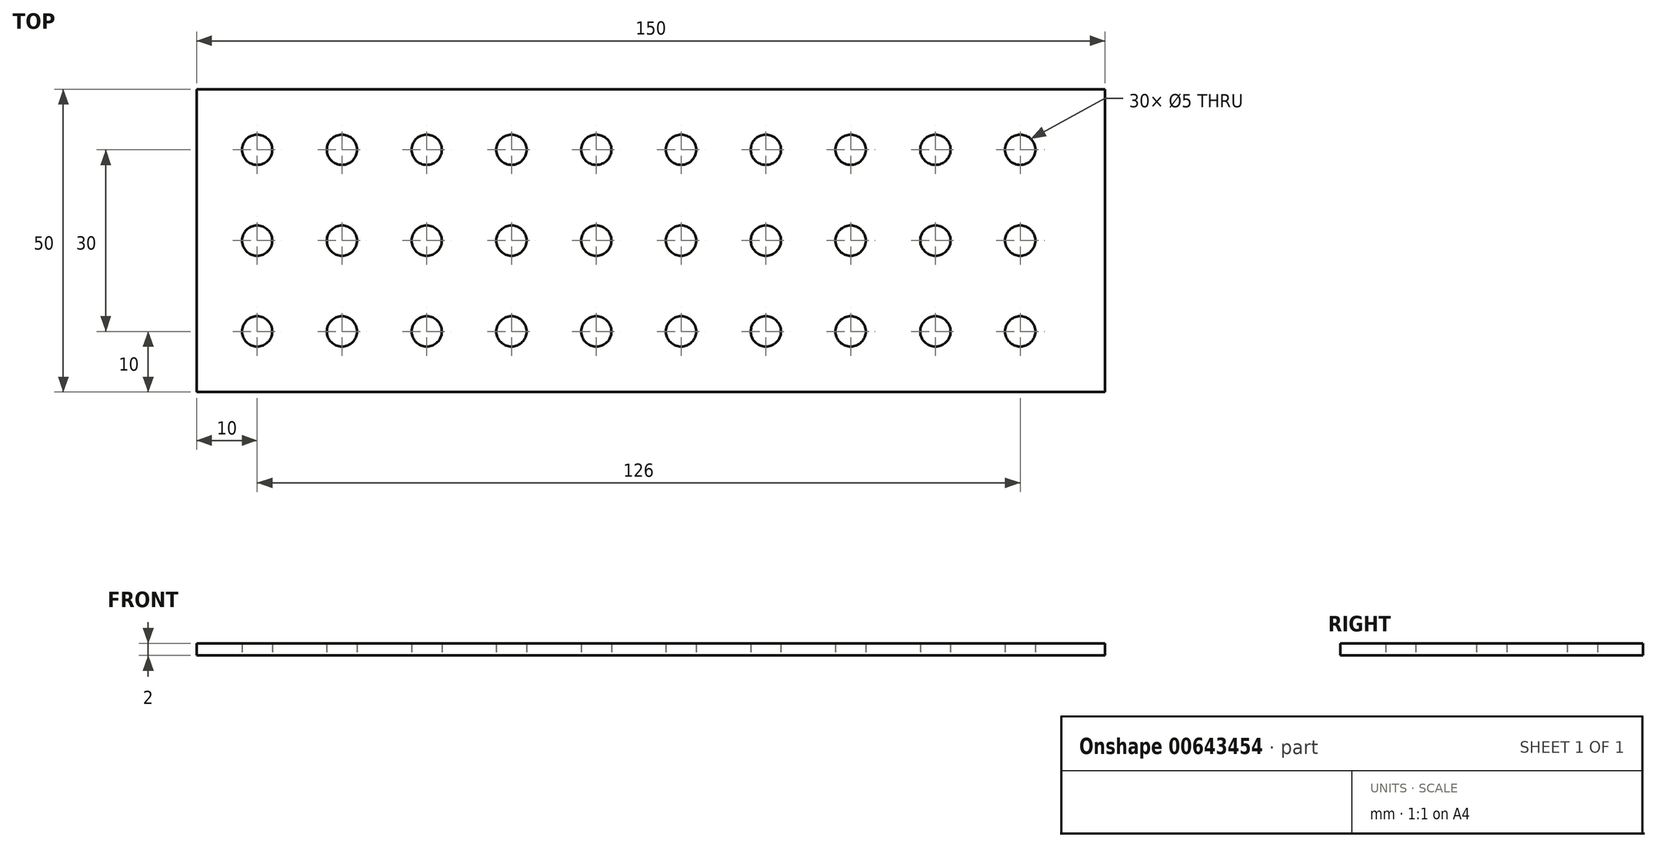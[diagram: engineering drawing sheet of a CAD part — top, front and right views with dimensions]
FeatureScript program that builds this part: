
annotation { "Feature Type Name" : "Feature", "Feature Type Description" : "" }
export const myFeature = defineFeature(function(context is Context, id is Id, definition is map)
    precondition{}
    {
        {
            var Q0;
            Q0=qCreatedBy(makeId("Top.planeOp"),FACE);
            var sketch = newSketch(context, id + "F0", { "sketchPlane" : qUnion([Q0])});
            skLineSegment(sketch, "E0.bottom", {"start": v(-75, 0) * mm, "end": v(75, 0) * mm});
            skLineSegment(sketch, "E0.top", {"start": v(-75, 50) * mm, "end": v(75, 50) * mm});
            skLineSegment(sketch, "E0.left", {"start": v(-75, 0) * mm, "end": v(-75, 50) * mm});
            skLineSegment(sketch, "E0.right", {"start": v(75, 0) * mm, "end": v(75, 50) * mm});
            skCircle(sketch, "E1", {"center": v(-65, 10) * mm, "radius": 2.5 * mm});
            skCircle(sketch, "E2.0.1.0", {"center": v(-65, 25) * mm, "radius": 2.5 * mm});
            skCircle(sketch, "E2.0.2.0", {"center": v(-65, 40) * mm, "radius": 2.5 * mm});
            skCircle(sketch, "E2.1.0.0", {"center": v(-51, 10) * mm, "radius": 2.5 * mm});
            skCircle(sketch, "E2.1.1.0", {"center": v(-51, 25) * mm, "radius": 2.5 * mm});
            skCircle(sketch, "E2.1.2.0", {"center": v(-51, 40) * mm, "radius": 2.5 * mm});
            skCircle(sketch, "E2.2.0.0", {"center": v(-37, 10) * mm, "radius": 2.5 * mm});
            skCircle(sketch, "E2.2.1.0", {"center": v(-37, 25) * mm, "radius": 2.5 * mm});
            skCircle(sketch, "E2.2.2.0", {"center": v(-37, 40) * mm, "radius": 2.5 * mm});
            skCircle(sketch, "E2.3.0.0", {"center": v(-23, 10) * mm, "radius": 2.5 * mm});
            skCircle(sketch, "E2.3.1.0", {"center": v(-23, 25) * mm, "radius": 2.5 * mm});
            skCircle(sketch, "E2.3.2.0", {"center": v(-23, 40) * mm, "radius": 2.5 * mm});
            skCircle(sketch, "E2.4.0.0", {"center": v(-9, 10) * mm, "radius": 2.5 * mm});
            skCircle(sketch, "E2.4.1.0", {"center": v(-9, 25) * mm, "radius": 2.5 * mm});
            skCircle(sketch, "E2.4.2.0", {"center": v(-9, 40) * mm, "radius": 2.5 * mm});
            skCircle(sketch, "E2.5.0.0", {"center": v(5, 10) * mm, "radius": 2.5 * mm});
            skCircle(sketch, "E2.5.1.0", {"center": v(5, 25) * mm, "radius": 2.5 * mm});
            skCircle(sketch, "E2.5.2.0", {"center": v(5, 40) * mm, "radius": 2.5 * mm});
            skCircle(sketch, "E2.6.0.0", {"center": v(19, 10) * mm, "radius": 2.5 * mm});
            skCircle(sketch, "E2.6.1.0", {"center": v(19, 25) * mm, "radius": 2.5 * mm});
            skCircle(sketch, "E2.6.2.0", {"center": v(19, 40) * mm, "radius": 2.5 * mm});
            skCircle(sketch, "E2.7.0.0", {"center": v(33, 10) * mm, "radius": 2.5 * mm});
            skCircle(sketch, "E2.7.1.0", {"center": v(33, 25) * mm, "radius": 2.5 * mm});
            skCircle(sketch, "E2.7.2.0", {"center": v(33, 40) * mm, "radius": 2.5 * mm});
            skCircle(sketch, "E2.8.0.0", {"center": v(47, 10) * mm, "radius": 2.5 * mm});
            skCircle(sketch, "E2.8.1.0", {"center": v(47, 25) * mm, "radius": 2.5 * mm});
            skCircle(sketch, "E2.8.2.0", {"center": v(47, 40) * mm, "radius": 2.5 * mm});
            skCircle(sketch, "E2.9.0.0", {"center": v(61, 10) * mm, "radius": 2.5 * mm});
            skCircle(sketch, "E2.9.1.0", {"center": v(61, 25) * mm, "radius": 2.5 * mm});
            skCircle(sketch, "E2.9.2.0", {"center": v(61, 40) * mm, "radius": 2.5 * mm});
            skLineSegment(sketch, "E2.direction1", {"start": v(-65, 10) * mm, "end": v(-51, 10) * mm, "construction": true});
            skLineSegment(sketch, "E2.direction2", {"start": v(-65, 10) * mm, "end": v(-65, 25) * mm, "construction": true});
            skSolve(sketch);
        }
        {
            var Q0;
            Q0=makeQuery(id+"F0.imprint","IMPRINT",FACE,{"disambiguationData":[TD([[makeQuery(id+"F0.imprint","IMPRINT",EDGE,{"derivedFrom":sQuery(id+"F0.wireOp",EDGE,"E0.bottom")}),1.0]])]});
            extrude(context, id + "F1", {"entities" : qUnion([Q0]), "depth" : 2 * mm, "offsetDistance" : 25 * mm});
        }
    });
